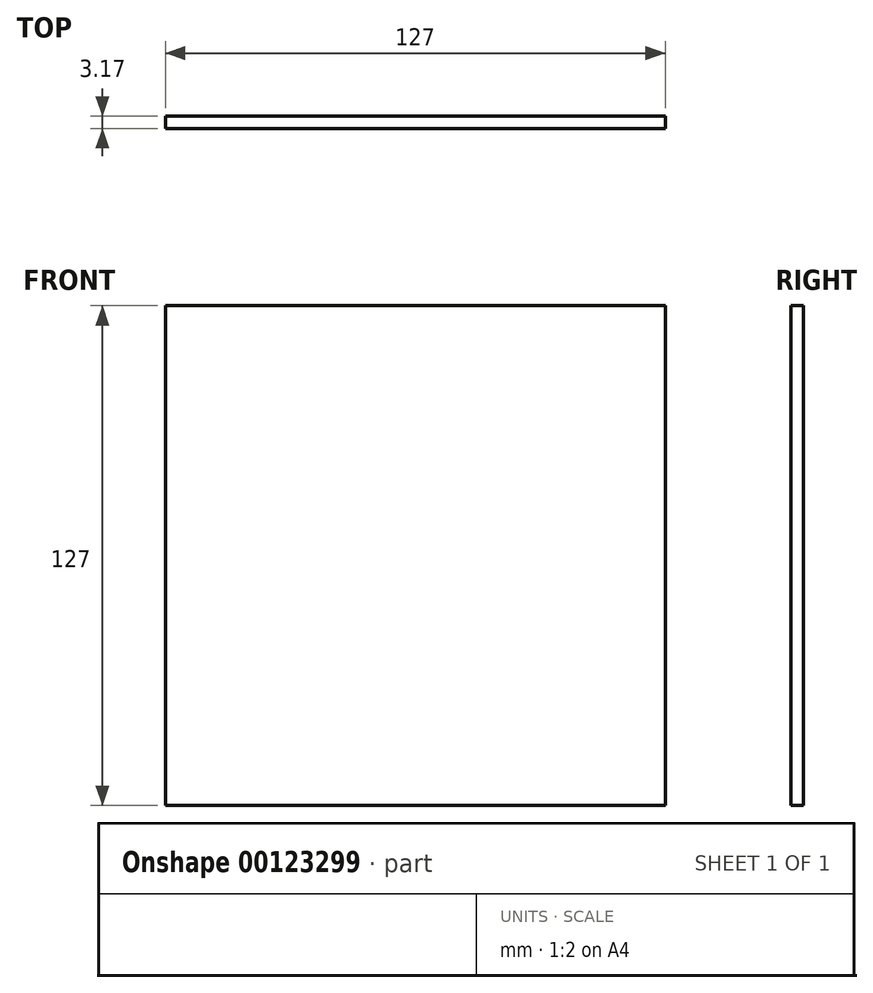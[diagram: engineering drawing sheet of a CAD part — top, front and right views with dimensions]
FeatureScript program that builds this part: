
annotation { "Feature Type Name" : "Feature", "Feature Type Description" : "" }
export const myFeature = defineFeature(function(context is Context, id is Id, definition is map)
    precondition{}
    {
        {
            var Q0;
            Q0=qCreatedBy(makeId("Front.planeOp"),FACE);
            var sketch = newSketch(context, id + "F0", { "sketchPlane" : qUnion([Q0])});
            skLineSegment(sketch, "E0.bottom", {"start": v(63.5, -63.5) * mm, "end": v(-63.5, -63.5) * mm});
            skLineSegment(sketch, "E0.top", {"start": v(63.5, 63.5) * mm, "end": v(-63.5, 63.5) * mm});
            skLineSegment(sketch, "E0.left", {"start": v(63.5, -63.5) * mm, "end": v(63.5, 63.5) * mm});
            skLineSegment(sketch, "E0.right", {"start": v(-63.5, -63.5) * mm, "end": v(-63.5, 63.5) * mm});
            skPoint(sketch, "E0.middle", {"position": v(0, 0) * mm});
            skSolve(sketch);
        }
        {
            var Q0;
            Q0 = qSketchRegion(id + "F0", true);
            extrude(context, id + "F1", {"entities" : qUnion([Q0]), "depth" : 3.17 * mm});
        }
    });
